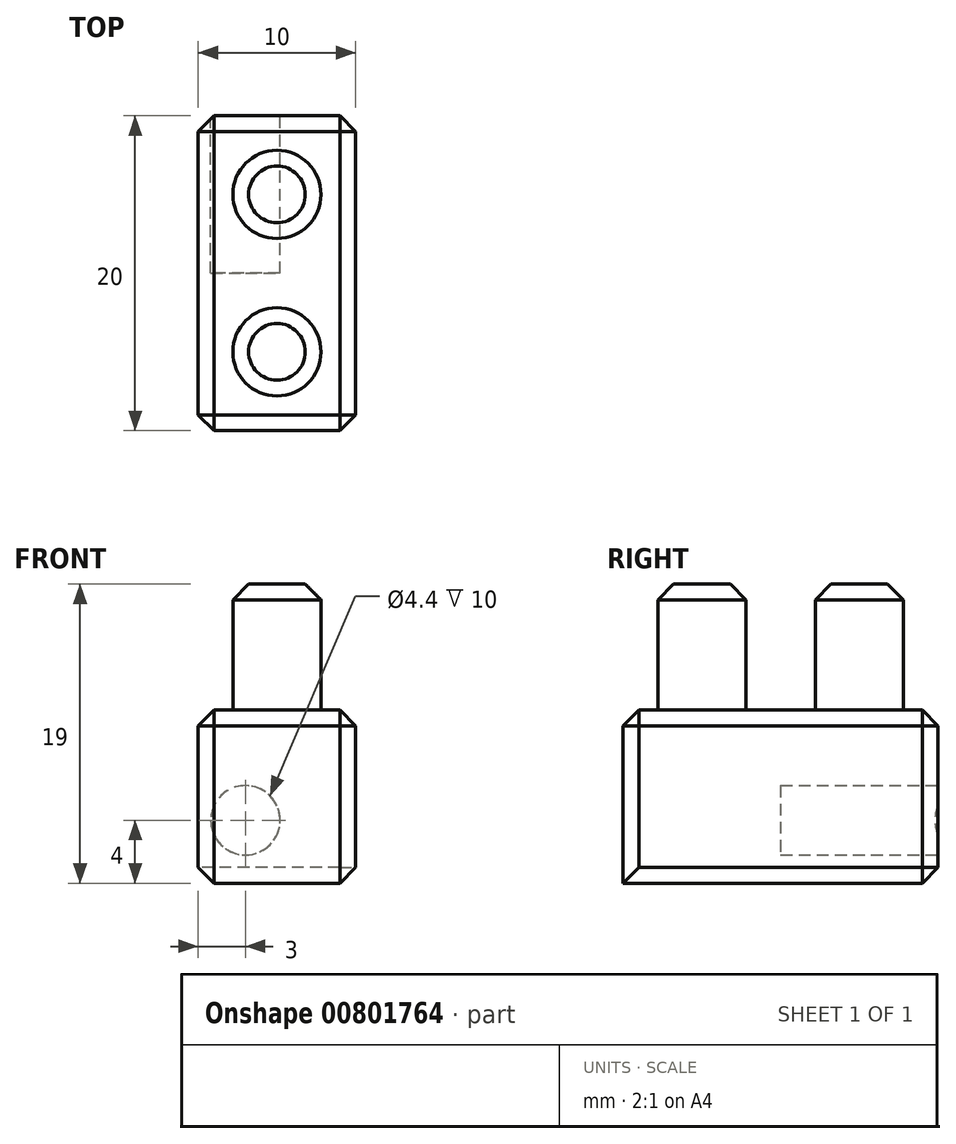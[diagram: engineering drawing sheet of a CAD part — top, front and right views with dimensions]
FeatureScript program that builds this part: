
annotation { "Feature Type Name" : "Feature", "Feature Type Description" : "" }
export const myFeature = defineFeature(function(context is Context, id is Id, definition is map)
    precondition{}
    {
        {
            var Q0;
            Q0=qCreatedBy(makeId("Top.planeOp"),FACE);
            var sketch = newSketch(context, id + "F0", { "sketchPlane" : qUnion([Q0])});
            skLineSegment(sketch, "E0.bottom", {"start": v(0, 0) * mm, "end": v(10, 0) * mm});
            skLineSegment(sketch, "E0.top", {"start": v(0, 20) * mm, "end": v(10, 20) * mm});
            skLineSegment(sketch, "E0.left", {"start": v(0, 0) * mm, "end": v(0, 20) * mm});
            skLineSegment(sketch, "E0.right", {"start": v(10, 0) * mm, "end": v(10, 20) * mm});
            skSolve(sketch);
        }
        {
            var Q0;
            Q0=makeQuery(id+"F0.imprint","IMPRINT",FACE,{"disambiguationData":[TD([[makeQuery(id+"F0.imprint","IMPRINT",EDGE,{"derivedFrom":sQuery(id+"F0.wireOp",EDGE,"E0.bottom")}),1.0]])]});
            extrude(context, id + "F1", {"entities" : qUnion([Q0]), "depth" : 11 * mm, "offsetDistance" : 25 * mm});
        }
        {
            var Q0;
            Q0=makeQuery(id+"F1.opExtrude","CAP_FACE",FACE,{"disambiguationData":[OSD([sQuery(id+"F0.wireOp",EDGE,"E0.bottom"),sQuery(id+"F0.wireOp",EDGE,"E0.top"),sQuery(id+"F0.wireOp",EDGE,"E0.left"),sQuery(id+"F0.wireOp",EDGE,"E0.right")])],"isStart":false});
            var sketch = newSketch(context, id + "F2", { "sketchPlane" : qUnion([Q0])});
            skCircle(sketch, "E1", {"center": v(5, 15) * mm, "radius": 2.8 * mm});
            skCircle(sketch, "E2.0.1.0", {"center": v(5, 5) * mm, "radius": 2.8 * mm});
            skLineSegment(sketch, "E2.direction1", {"start": v(5, 15) * mm, "end": v(30, 15) * mm, "construction": true});
            skLineSegment(sketch, "E2.direction2", {"start": v(5, 15) * mm, "end": v(5, 5) * mm, "construction": true});
            skSolve(sketch);
        }
        {
            var Q0;
            Q0=makeQuery(id+"F2.imprint","IMPRINT",FACE,{"disambiguationData":[TD([[makeQuery(id+"F2.imprint","IMPRINT",EDGE,{"derivedFrom":sQuery(id+"F2.wireOp",EDGE,"E1")}),1.0]])]});
            var Q1;
            Q1=makeQuery(id+"F2.imprint","IMPRINT",FACE,{"disambiguationData":[TD([[makeQuery(id+"F2.imprint","IMPRINT",EDGE,{"derivedFrom":sQuery(id+"F2.wireOp",EDGE,"E2.0.1.0")}),1.0]])]});
            extrude(context, id + "F3", {"entities" : qUnion([Q0, Q1]), "operationType" : NewBodyOperationType.ADD, "depth" : 8 * mm, "offsetDistance" : 25 * mm});
        }
        {
            var Q0;
            Q0=makeQuery(id+"F1.opExtrude","SWEPT_FACE",FACE,{"disambiguationData":[OSD([sQuery(id+"F0.wireOp",EDGE,"E0.top")])]});
            var sketch = newSketch(context, id + "F4", { "sketchPlane" : qUnion([Q0])});
            skCircle(sketch, "E3", {"center": v(-3, 4) * mm, "radius": 2.2 * mm});
            skSolve(sketch);
        }
        {
            var Q0;
            Q0=makeQuery(id+"F4.imprint","IMPRINT",FACE,{"disambiguationData":[TD([[makeQuery(id+"F4.imprint","IMPRINT",EDGE,{"derivedFrom":sQuery(id+"F4.wireOp",EDGE,"E3")}),1.0]])]});
            extrude(context, id + "F5", {"entities" : qUnion([Q0]), "operationType" : NewBodyOperationType.REMOVE, "oppositeDirection" : true, "depth" : 10 * mm, "offsetDistance" : 25 * mm});
        }
        {
            var Q0;
            Q0=makeQuery(id+"F1.opExtrude","CAP_EDGE",EDGE,{"disambiguationData":[OSD([sQuery(id+"F0.wireOp",EDGE,"E0.left")])],"isStart":true});
            var Q1;
            Q1=makeQuery(id+"F1.opExtrude","CAP_EDGE",EDGE,{"disambiguationData":[OSD([sQuery(id+"F0.wireOp",EDGE,"E0.right")])],"isStart":true});
            var Q2;
            Q2=makeQuery(id+"F1.opExtrude","SWEPT_EDGE",EDGE,{"disambiguationData":[OSD([sQuery(id+"F0.wireOp",EDGE,"E0.bottom"),sQuery(id+"F0.wireOp",EDGE,"E0.right")])]});
            var Q3;
            Q3=makeQuery(id+"F1.opExtrude","SWEPT_EDGE",EDGE,{"disambiguationData":[OSD([sQuery(id+"F0.wireOp",EDGE,"E0.bottom"),sQuery(id+"F0.wireOp",EDGE,"E0.left")])]});
            var Q4;
            Q4=makeQuery(id+"F1.opExtrude","CAP_EDGE",EDGE,{"disambiguationData":[OSD([sQuery(id+"F0.wireOp",EDGE,"E0.bottom")])],"isStart":false});
            var Q5;
            Q5=makeQuery(id+"F1.opExtrude","CAP_EDGE",EDGE,{"disambiguationData":[OSD([sQuery(id+"F0.wireOp",EDGE,"E0.right")])],"isStart":false});
            var Q6;
            Q6=makeQuery(id+"F1.opExtrude","SWEPT_EDGE",EDGE,{"disambiguationData":[OSD([sQuery(id+"F0.wireOp",EDGE,"E0.top"),sQuery(id+"F0.wireOp",EDGE,"E0.right")])]});
            var Q7;
            Q7=makeQuery(id+"F1.opExtrude","CAP_EDGE",EDGE,{"disambiguationData":[OSD([sQuery(id+"F0.wireOp",EDGE,"E0.top")])],"isStart":true});
            var Q8;
            Q8=makeQuery(id+"F1.opExtrude","SWEPT_EDGE",EDGE,{"disambiguationData":[OSD([sQuery(id+"F0.wireOp",EDGE,"E0.top"),sQuery(id+"F0.wireOp",EDGE,"E0.left")])]});
            var Q9;
            Q9=makeQuery(id+"F1.opExtrude","CAP_EDGE",EDGE,{"disambiguationData":[OSD([sQuery(id+"F0.wireOp",EDGE,"E0.left")])],"isStart":false});
            var Q10;
            Q10=makeQuery(id+"F3.opExtrude","CAP_EDGE",EDGE,{"disambiguationData":[OSD([sQuery(id+"F2.wireOp",EDGE,"E1")])],"isStart":false});
            var Q11;
            Q11=makeQuery(id+"F3.opExtrude","CAP_EDGE",EDGE,{"disambiguationData":[OSD([sQuery(id+"F2.wireOp",EDGE,"E2.0.1.0")])],"isStart":false});
            var Q12;
            Q12=makeQuery(id+"F1.opExtrude","CAP_EDGE",EDGE,{"disambiguationData":[OSD([sQuery(id+"F0.wireOp",EDGE,"E0.top")])],"isStart":false});
            chamfer(context, id + "F6", {"entities" : qUnion([Q0, Q1, Q2, Q3, Q4, Q5, Q6, Q7, Q8, Q9, Q10, Q11, Q12]), "width" : 1 * mm, "tangentPropagation" : true});
        }
    });
